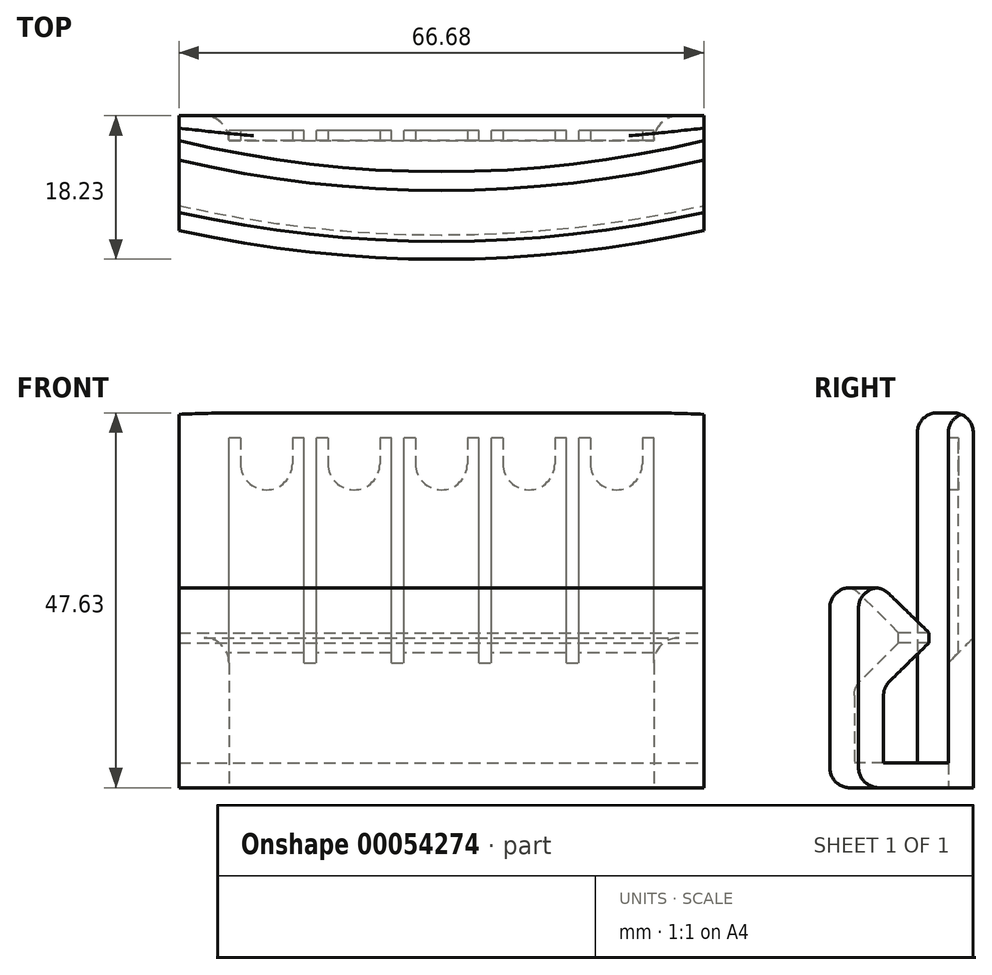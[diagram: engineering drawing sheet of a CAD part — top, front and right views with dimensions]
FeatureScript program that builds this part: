
annotation { "Feature Type Name" : "Feature", "Feature Type Description" : "" }
export const myFeature = defineFeature(function(context is Context, id is Id, definition is map)
    precondition{}
    {
        {
            var Q0;
            Q0=qCreatedBy(makeId("Top.planeOp"),FACE);
            var sketch = newSketch(context, id + "F0", { "sketchPlane" : qUnion([Q0])});
            skCircle(sketch, "E0", {"center": v(0, 0) * mm, "radius": 150.81 * mm, "construction": true});
            skCircle(sketch, "E1", {"center": v(0, 0) * mm, "radius": 142.88 * mm, "construction": true});
            skLineSegment(sketch, "E2", {"start": v(0, 0) * mm, "end": v(0, -150.81) * mm, "construction": true});
            skLineSegment(sketch, "E3", {"start": v(-17.46, -138.93) * mm, "end": v(-15.88, -138.93) * mm});
            skLineSegment(sketch, "E4", {"start": v(-15.88, -138.93) * mm, "end": v(-6.35, -138.93) * mm});
            skLineSegment(sketch, "E5", {"start": v(-6.35, -138.93) * mm, "end": v(-4.76, -138.93) * mm});
            skLineSegment(sketch, "E6", {"start": v(-4.76, -138.93) * mm, "end": v(4.76, -138.93) * mm});
            skLineSegment(sketch, "E7", {"start": v(4.76, -138.93) * mm, "end": v(6.35, -138.93) * mm});
            skLineSegment(sketch, "E8", {"start": v(6.35, -138.93) * mm, "end": v(15.88, -138.93) * mm});
            skLineSegment(sketch, "E9", {"start": v(15.88, -138.93) * mm, "end": v(17.46, -138.93) * mm});
            skLineSegment(sketch, "E10", {"start": v(17.46, -138.93) * mm, "end": v(26.99, -138.93) * mm});
            skLineSegment(sketch, "E11", {"start": v(26.99, -138.93) * mm, "end": v(33.34, -138.93) * mm});
            skLineSegment(sketch, "E12", {"start": v(-17.46, -138.93) * mm, "end": v(-26.99, -138.93) * mm});
            skLineSegment(sketch, "E13", {"start": v(-26.99, -138.93) * mm, "end": v(-33.34, -138.93) * mm});
            skLineSegment(sketch, "E14", {"start": v(-33.34, -138.93) * mm, "end": v(-33.34, -150.34) * mm});
            skLineSegment(sketch, "E15", {"start": v(33.34, -138.93) * mm, "end": v(33.34, -150.34) * mm});
            skArc(sketch, "E16", {"start": v(-33.34, -150.34) * mm, "mid": v(0, -153.99) * mm, "end": v(33.34, -150.34) * mm});
            skCircle(sketch, "E17.0", {"center": v(0, 0) * mm, "radius": 145.26 * mm, "construction": true});
            skSolve(sketch);
        }
        {
            var Q0;
            Q0 = qSketchRegion(id + "F0", true);
            extrude(context, id + "F1", {"entities" : qUnion([Q0]), "depth" : 3.17 * mm, "offsetDistance" : 25.4 * mm});
        }
        {
            var Q0;
            Q0=makeQuery(id+"F1.opExtrude","CAP_FACE",FACE,{"disambiguationData":[OSD([sQuery(id+"F0.wireOp",EDGE,"E3"),sQuery(id+"F0.wireOp",EDGE,"E4"),sQuery(id+"F0.wireOp",EDGE,"E5"),sQuery(id+"F0.wireOp",EDGE,"E6"),sQuery(id+"F0.wireOp",EDGE,"E7"),sQuery(id+"F0.wireOp",EDGE,"E8"),sQuery(id+"F0.wireOp",EDGE,"E9"),sQuery(id+"F0.wireOp",EDGE,"E10"),sQuery(id+"F0.wireOp",EDGE,"E11"),sQuery(id+"F0.wireOp",EDGE,"E12"),sQuery(id+"F0.wireOp",EDGE,"E13"),sQuery(id+"F0.wireOp",EDGE,"E14"),sQuery(id+"F0.wireOp",EDGE,"E15"),sQuery(id+"F0.wireOp",EDGE,"E16")])],"isStart":false});
            var sketch = newSketch(context, id + "F2", { "sketchPlane" : qUnion([Q0])});
            skLineSegment(sketch, "E18", {"start": v(-33.34, -150.34) * mm, "end": v(-33.34, -147.16) * mm});
            skLineSegment(sketch, "E19", {"start": v(33.34, -150.34) * mm, "end": v(33.34, -147.16) * mm});
            skArc(sketch, "E20", {"start": v(-33.34, -147.16) * mm, "mid": v(0, -150.89) * mm, "end": v(33.34, -147.16) * mm});
            skArc(sketch, "E21", {"start": v(-33.34, -150.34) * mm, "mid": v(0, -153.99) * mm, "end": v(33.34, -150.34) * mm});
            skSolve(sketch);
        }
        {
            var Q0;
            Q0 = qSketchRegion(id + "F2", true);
            extrude(context, id + "F3", {"entities" : qUnion([Q0]), "operationType" : NewBodyOperationType.ADD, "depth" : 22.22 * mm, "offsetDistance" : 25.4 * mm});
        }
        {
            var Q0;
            Q0=makeQuery(id+"F3.opExtrude","CAP_FACE",FACE,{"disambiguationData":[OSD([sQuery(id+"F2.wireOp",EDGE,"E18"),sQuery(id+"F2.wireOp",EDGE,"E19"),sQuery(id+"F2.wireOp",EDGE,"E20"),sQuery(id+"F2.wireOp",EDGE,"E21")])],"isStart":false});
            var sketch = newSketch(context, id + "F4", { "sketchPlane" : qUnion([Q0])});
            skLineSegment(sketch, "E22", {"start": v(-33.34, -147.16) * mm, "end": v(-33.34, -141.38) * mm});
            skLineSegment(sketch, "E23", {"start": v(33.34, -147.16) * mm, "end": v(33.34, -141.38) * mm});
            skArc(sketch, "E24.0", {"start": v(-33.34, -147.16) * mm, "mid": v(0, -150.89) * mm, "end": v(33.34, -147.16) * mm});
            skArc(sketch, "E25", {"start": v(-33.34, -141.38) * mm, "mid": v(0, -145.26) * mm, "end": v(33.34, -141.38) * mm});
            skSolve(sketch);
        }
        {
            var Q0;
            Q0 = qSketchRegion(id + "F4", true);
            extrude(context, id + "F5", {"entities" : qUnion([Q0]), "operationType" : NewBodyOperationType.ADD, "oppositeDirection" : true, "depth" : 12.7 * mm, "offsetDistance" : 25.4 * mm});
        }
        {
            var Q0;
            Q0=makeQuery(id+"F5.opExtrude","CAP_EDGE",EDGE,{"disambiguationData":[OSD([sQuery(id+"F4.wireOp",EDGE,"E25")])],"isStart":false});
            var Q1;
            Q1=makeQuery(id+"F5.opExtrude","CAP_EDGE",EDGE,{"disambiguationData":[OSD([sQuery(id+"F4.wireOp",EDGE,"E25")])],"isStart":true});
            chamfer(context, id + "F6", {"entities" : qUnion([Q0, Q1]), "width" : 5.7 * mm, "tangentPropagation" : true});
        }
        {
            var Q0;
            Q0=makeQuery(id+"F1.opExtrude","CAP_FACE",FACE,{"disambiguationData":[OSD([sQuery(id+"F0.wireOp",EDGE,"E3"),sQuery(id+"F0.wireOp",EDGE,"E4"),sQuery(id+"F0.wireOp",EDGE,"E5"),sQuery(id+"F0.wireOp",EDGE,"E6"),sQuery(id+"F0.wireOp",EDGE,"E7"),sQuery(id+"F0.wireOp",EDGE,"E8"),sQuery(id+"F0.wireOp",EDGE,"E9"),sQuery(id+"F0.wireOp",EDGE,"E10"),sQuery(id+"F0.wireOp",EDGE,"E11"),sQuery(id+"F0.wireOp",EDGE,"E12"),sQuery(id+"F0.wireOp",EDGE,"E13"),sQuery(id+"F0.wireOp",EDGE,"E14"),sQuery(id+"F0.wireOp",EDGE,"E15"),sQuery(id+"F0.wireOp",EDGE,"E16")])],"isStart":false});
            var sketch = newSketch(context, id + "F7", { "sketchPlane" : qUnion([Q0])});
            skLineSegment(sketch, "E26", {"start": v(-33.34, -138.93) * mm, "end": v(33.34, -138.93) * mm});
            skArc(sketch, "E27", {"start": v(-33.34, -138.93) * mm, "mid": v(0, -142.88) * mm, "end": v(33.34, -138.93) * mm});
            skSolve(sketch);
        }
        {
            var Q0;
            Q0 = qSketchRegion(id + "F7", true);
            extrude(context, id + "F8", {"entities" : qUnion([Q0]), "operationType" : NewBodyOperationType.ADD, "depth" : 44.45 * mm, "offsetDistance" : 25.4 * mm});
        }
        {
            var Q0;
            Q0=makeQuery(id+"F5.boolean.opBoolean","MERGE",FACE,{"derivedFrom":[makeQuery(id+"F3.boolean.opBoolean","MERGE",FACE,{"derivedFrom":[makeQuery(id+"F1.opExtrude","SWEPT_FACE",FACE,{"disambiguationData":[OSD([sQuery(id+"F0.wireOp",EDGE,"E15")])]}),makeQuery(id+"F3.opExtrude","SWEPT_FACE",FACE,{"disambiguationData":[OSD([sQuery(id+"F2.wireOp",EDGE,"E19")])]})]}),makeQuery(id+"F5.opExtrude","SWEPT_FACE",FACE,{"disambiguationData":[OSD([sQuery(id+"F4.wireOp",EDGE,"E23")])]})]});
            var sketch = newSketch(context, id + "F9", { "sketchPlane" : qUnion([Q0])});
            skLineSegment(sketch, "E28", {"start": v(-138.93, 15.88) * mm, "end": v(-138.93, 47.62) * mm});
            skLineSegment(sketch, "E29", {"start": v(-138.93, 47.62) * mm, "end": v(-135.76, 47.62) * mm});
            skLineSegment(sketch, "E30", {"start": v(-135.76, 47.62) * mm, "end": v(-135.76, 19.05) * mm});
            skLineSegment(sketch, "E31", {"start": v(-135.76, 19.05) * mm, "end": v(-138.93, 15.88) * mm});
            skSolve(sketch);
        }
        {
            var Q0;
            Q0 = qSketchRegion(id + "F9", true);
            var Q1;
            Q1=makeQuery(id+"F5.boolean.opBoolean","MERGE",FACE,{"derivedFrom":[makeQuery(id+"F3.boolean.opBoolean","MERGE",FACE,{"derivedFrom":[makeQuery(id+"F1.opExtrude","SWEPT_FACE",FACE,{"disambiguationData":[OSD([sQuery(id+"F0.wireOp",EDGE,"E14")])]}),makeQuery(id+"F3.opExtrude","SWEPT_FACE",FACE,{"disambiguationData":[OSD([sQuery(id+"F2.wireOp",EDGE,"E18")])]})]}),makeQuery(id+"F5.opExtrude","SWEPT_FACE",FACE,{"disambiguationData":[OSD([sQuery(id+"F4.wireOp",EDGE,"E22")])]})]});
            extrude(context, id + "F10", {"entities" : qUnion([Q0]), "operationType" : NewBodyOperationType.ADD, "endBound" : BoundingType.UP_TO_SURFACE, "oppositeDirection" : true, "depth" : 25.4 * mm, "endBoundEntityFace" : qUnion([Q1]), "offsetDistance" : 25.4 * mm});
        }
        {
            var Q0;
            Q0=makeQuery(id+"F1.opExtrude","CAP_EDGE",EDGE,{"disambiguationData":[OSD([sQuery(id+"F0.wireOp",EDGE,"E16")])],"isStart":true});
            var Q1;
            {var subQ0=sQuery(id+"F4.wireOp",EDGE,"E25");Q1=makeQuery(id+"F6.opChamfer","BLEND_EDGE",EDGE,{"blendedFrom":[makeQuery(id+"F5.opExtrude","CAP_EDGE",EDGE,{"disambiguationData":[OSD([subQ0])],"isStart":true}),makeQuery(id+"F5.boolean.opBoolean","MERGE",FACE,{"derivedFrom":[makeQuery(id+"F3.opExtrude","CAP_FACE",FACE,{"disambiguationData":[OSD([sQuery(id+"F2.wireOp",EDGE,"E18"),sQuery(id+"F2.wireOp",EDGE,"E19"),sQuery(id+"F2.wireOp",EDGE,"E20"),sQuery(id+"F2.wireOp",EDGE,"E21")])],"isStart":false}),makeQuery(id+"F5.opExtrude","CAP_FACE",FACE,{"disambiguationData":[OSD([sQuery(id+"F4.wireOp",EDGE,"E22"),sQuery(id+"F4.wireOp",EDGE,"E23"),sQuery(id+"F4.wireOp",EDGE,"E24.0"),subQ0])],"isStart":true})]})],"blendedInto":[makeQuery(id+"F5.boolean.opBoolean","MERGE",FACE,{"derivedFrom":[makeQuery(id+"F3.opExtrude","CAP_FACE",FACE,{"disambiguationData":[OSD([sQuery(id+"F2.wireOp",EDGE,"E18"),sQuery(id+"F2.wireOp",EDGE,"E19"),sQuery(id+"F2.wireOp",EDGE,"E20"),sQuery(id+"F2.wireOp",EDGE,"E21")])],"isStart":false}),makeQuery(id+"F5.opExtrude","CAP_FACE",FACE,{"disambiguationData":[OSD([sQuery(id+"F4.wireOp",EDGE,"E22"),sQuery(id+"F4.wireOp",EDGE,"E23"),sQuery(id+"F4.wireOp",EDGE,"E24.0"),subQ0])],"isStart":true})]})]});}
            var Q2;
            Q2=makeQuery(id+"F3.opExtrude","CAP_EDGE",EDGE,{"disambiguationData":[OSD([sQuery(id+"F2.wireOp",EDGE,"E21")])],"isStart":false});
            var Q3;
            Q3=makeQuery(id+"F6.opChamfer","BLEND_EDGE",EDGE,{"blendedFrom":[makeQuery(id+"F5.opExtrude","CAP_EDGE",EDGE,{"disambiguationData":[OSD([sQuery(id+"F4.wireOp",EDGE,"E25")])],"isStart":false}),makeQuery(id+"F3.opExtrude","SWEPT_FACE",FACE,{"disambiguationData":[OSD([sQuery(id+"F2.wireOp",EDGE,"E20")])]})],"blendedInto":[makeQuery(id+"F3.opExtrude","SWEPT_FACE",FACE,{"disambiguationData":[OSD([sQuery(id+"F2.wireOp",EDGE,"E20")])]})]});
            var Q4;
            Q4=makeQuery(id+"F8.opExtrude","CAP_EDGE",EDGE,{"disambiguationData":[OSD([sQuery(id+"F7.wireOp",EDGE,"E27")])],"isStart":false});
            var Q5;
            Q5=makeQuery(id+"F10.opExtrude","SWEPT_EDGE",EDGE,{"disambiguationData":[OSD([sQuery(id+"F9.wireOp",EDGE,"E29"),sQuery(id+"F9.wireOp",EDGE,"E30")])]});
            fillet(context, id + "F11", {"entities" : qUnion([Q0, Q1, Q2, Q3, Q4, Q5]), "tangentPropagation" : true, "radius" : 2.54 * mm, "defaultsChanged" : false, "vertexSettings" : [], "allowEdgeOverflow" : false});
        }
        {
            var Q0;
            Q0=makeQuery(id+"F8.boolean.opBoolean","MERGE",FACE,{"derivedFrom":[makeQuery(id+"F1.opExtrude","SWEPT_FACE",FACE,{"disambiguationData":[OSD([sQuery(id+"F0.wireOp",EDGE,"E3"),sQuery(id+"F0.wireOp",EDGE,"E4"),sQuery(id+"F0.wireOp",EDGE,"E5"),sQuery(id+"F0.wireOp",EDGE,"E6"),sQuery(id+"F0.wireOp",EDGE,"E7"),sQuery(id+"F0.wireOp",EDGE,"E8"),sQuery(id+"F0.wireOp",EDGE,"E9"),sQuery(id+"F0.wireOp",EDGE,"E10"),sQuery(id+"F0.wireOp",EDGE,"E11"),sQuery(id+"F0.wireOp",EDGE,"E12"),sQuery(id+"F0.wireOp",EDGE,"E13")])]}),makeQuery(id+"F8.opExtrude","SWEPT_FACE",FACE,{"disambiguationData":[OSD([sQuery(id+"F7.wireOp",EDGE,"E26")])]})]});
            var sketch = newSketch(context, id + "F12", { "sketchPlane" : qUnion([Q0])});
            skLineSegment(sketch, "E32.bottom", {"start": v(-33.34, 0) * mm, "end": v(-26.99, 0) * mm});
            skLineSegment(sketch, "E32.top", {"start": v(-33.34, 19.05) * mm, "end": v(-26.99, 19.05) * mm});
            skLineSegment(sketch, "E32.left", {"start": v(-33.34, 0) * mm, "end": v(-33.34, 19.05) * mm});
            skLineSegment(sketch, "E32.right", {"start": v(-26.99, 0) * mm, "end": v(-26.99, 19.05) * mm});
            skLineSegment(sketch, "E33.bottom", {"start": v(-17.46, 0) * mm, "end": v(-15.88, 0) * mm});
            skLineSegment(sketch, "E33.top", {"start": v(-17.46, 19.05) * mm, "end": v(-15.88, 19.05) * mm});
            skLineSegment(sketch, "E33.left", {"start": v(-17.46, 0) * mm, "end": v(-17.46, 19.05) * mm});
            skLineSegment(sketch, "E33.right", {"start": v(-15.88, 0) * mm, "end": v(-15.88, 19.05) * mm});
            skLineSegment(sketch, "E34.bottom", {"start": v(-6.35, 0) * mm, "end": v(-4.76, 0) * mm});
            skLineSegment(sketch, "E34.top", {"start": v(-6.35, 19.05) * mm, "end": v(-4.76, 19.05) * mm});
            skLineSegment(sketch, "E34.left", {"start": v(-6.35, 0) * mm, "end": v(-6.35, 19.05) * mm});
            skLineSegment(sketch, "E34.right", {"start": v(-4.76, 0) * mm, "end": v(-4.76, 19.05) * mm});
            skLineSegment(sketch, "E35.bottom", {"start": v(4.76, 0) * mm, "end": v(6.35, 0) * mm});
            skLineSegment(sketch, "E35.top", {"start": v(4.76, 19.05) * mm, "end": v(6.35, 19.05) * mm});
            skLineSegment(sketch, "E35.left", {"start": v(4.76, 0) * mm, "end": v(4.76, 19.05) * mm});
            skLineSegment(sketch, "E35.right", {"start": v(6.35, 0) * mm, "end": v(6.35, 19.05) * mm});
            skLineSegment(sketch, "E36.bottom", {"start": v(15.88, 0) * mm, "end": v(17.46, 0) * mm});
            skLineSegment(sketch, "E36.top", {"start": v(15.88, 19.05) * mm, "end": v(17.46, 19.05) * mm});
            skLineSegment(sketch, "E36.left", {"start": v(15.88, 0) * mm, "end": v(15.88, 19.05) * mm});
            skLineSegment(sketch, "E36.right", {"start": v(17.46, 0) * mm, "end": v(17.46, 19.05) * mm});
            skLineSegment(sketch, "E37.bottom", {"start": v(26.99, 0) * mm, "end": v(33.34, 0) * mm});
            skLineSegment(sketch, "E37.top", {"start": v(26.99, 19.05) * mm, "end": v(33.34, 19.05) * mm});
            skLineSegment(sketch, "E37.left", {"start": v(26.99, 0) * mm, "end": v(26.99, 19.05) * mm});
            skLineSegment(sketch, "E37.right", {"start": v(33.34, 0) * mm, "end": v(33.34, 19.05) * mm});
            skLineSegment(sketch, "E38", {"start": v(-26.99, 0) * mm, "end": v(-17.46, 0) * mm, "construction": true});
            skLineSegment(sketch, "E39", {"start": v(-15.88, 0) * mm, "end": v(-6.35, 0) * mm, "construction": true});
            skLineSegment(sketch, "E40", {"start": v(-4.76, 0) * mm, "end": v(4.76, 0) * mm, "construction": true});
            skLineSegment(sketch, "E41", {"start": v(6.35, 0) * mm, "end": v(15.88, 0) * mm, "construction": true});
            skLineSegment(sketch, "E42", {"start": v(17.46, 0) * mm, "end": v(26.99, 0) * mm, "construction": true});
            skSolve(sketch);
        }
        {
            var Q0;
            Q0=makeQuery(id+"F8.boolean.opBoolean","MERGE",FACE,{"derivedFrom":[makeQuery(id+"F1.opExtrude","SWEPT_FACE",FACE,{"disambiguationData":[OSD([sQuery(id+"F0.wireOp",EDGE,"E3"),sQuery(id+"F0.wireOp",EDGE,"E4"),sQuery(id+"F0.wireOp",EDGE,"E5"),sQuery(id+"F0.wireOp",EDGE,"E6"),sQuery(id+"F0.wireOp",EDGE,"E7"),sQuery(id+"F0.wireOp",EDGE,"E8"),sQuery(id+"F0.wireOp",EDGE,"E9"),sQuery(id+"F0.wireOp",EDGE,"E10"),sQuery(id+"F0.wireOp",EDGE,"E11"),sQuery(id+"F0.wireOp",EDGE,"E12"),sQuery(id+"F0.wireOp",EDGE,"E13")])]}),makeQuery(id+"F8.opExtrude","SWEPT_FACE",FACE,{"disambiguationData":[OSD([sQuery(id+"F7.wireOp",EDGE,"E26")])]})]});
            var sketch = newSketch(context, id + "F13", { "sketchPlane" : qUnion([Q0])});
            skLineSegment(sketch, "E43", {"start": v(-26.99, 20.64) * mm, "end": v(-26.99, 44.45) * mm, "construction": true});
            skLineSegment(sketch, "E44", {"start": v(-26.99, 44.45) * mm, "end": v(-17.46, 20.64) * mm, "construction": true});
            skLineSegment(sketch, "E45", {"start": v(-26.99, 20.64) * mm, "end": v(-17.46, 20.64) * mm, "construction": true});
            skLineSegment(sketch, "E46.bottom", {"start": v(-26.99, 15.88) * mm, "end": v(-17.46, 15.88) * mm});
            skLineSegment(sketch, "E46.top", {"start": v(-26.99, 44.45) * mm, "end": v(-25.53, 44.45) * mm});
            skLineSegment(sketch, "E46.left", {"start": v(-26.99, 15.88) * mm, "end": v(-26.99, 44.45) * mm});
            skLineSegment(sketch, "E46.right", {"start": v(-17.46, 15.88) * mm, "end": v(-17.46, 44.45) * mm});
            skArc(sketch, "E47", {"start": v(-25.53, 41.15) * mm, "mid": v(-22.23, 37.85) * mm, "end": v(-18.92, 41.15) * mm});
            skPoint(sketch, "E47.centerSnap0", {"position": v(-22.23, 44.45) * mm});
            skLineSegment(sketch, "E48", {"start": v(-22.23, 44.45) * mm, "end": v(-22.23, 41.15) * mm, "construction": true});
            skLineSegment(sketch, "E49.left", {"start": v(-25.53, 44.45) * mm, "end": v(-25.53, 41.15) * mm});
            skLineSegment(sketch, "E49.right", {"start": v(-18.92, 44.45) * mm, "end": v(-18.92, 41.15) * mm});
            skLineSegment(sketch, "E50.trimOffspring", {"start": v(-18.92, 44.45) * mm, "end": v(-17.46, 44.45) * mm});
            skLineSegment(sketch, "E51.1.0.0", {"start": v(-15.88, 15.88) * mm, "end": v(-6.35, 15.88) * mm});
            skLineSegment(sketch, "E51.1.0.1", {"start": v(-6.35, 15.88) * mm, "end": v(-6.35, 44.45) * mm});
            skLineSegment(sketch, "E51.1.0.2", {"start": v(-15.88, 15.88) * mm, "end": v(-15.88, 44.45) * mm});
            skLineSegment(sketch, "E51.1.0.3", {"start": v(-7.81, 44.45) * mm, "end": v(-6.35, 44.45) * mm});
            skLineSegment(sketch, "E51.1.0.4", {"start": v(-7.81, 44.45) * mm, "end": v(-7.81, 41.15) * mm});
            skArc(sketch, "E51.1.0.5", {"start": v(-14.41, 41.15) * mm, "mid": v(-11.11, 37.85) * mm, "end": v(-7.81, 41.15) * mm});
            skLineSegment(sketch, "E51.1.0.6", {"start": v(-14.41, 44.45) * mm, "end": v(-14.41, 41.15) * mm});
            skLineSegment(sketch, "E51.1.0.7", {"start": v(-15.88, 44.45) * mm, "end": v(-14.41, 44.45) * mm});
            skLineSegment(sketch, "E51.2.0.0", {"start": v(-4.76, 15.88) * mm, "end": v(4.76, 15.88) * mm});
            skLineSegment(sketch, "E51.2.0.1", {"start": v(4.76, 15.88) * mm, "end": v(4.76, 44.45) * mm});
            skLineSegment(sketch, "E51.2.0.2", {"start": v(-4.76, 15.88) * mm, "end": v(-4.76, 44.45) * mm});
            skLineSegment(sketch, "E51.2.0.3", {"start": v(3.3, 44.45) * mm, "end": v(4.76, 44.45) * mm});
            skLineSegment(sketch, "E51.2.0.4", {"start": v(3.3, 44.45) * mm, "end": v(3.3, 41.15) * mm});
            skArc(sketch, "E51.2.0.5", {"start": v(-3.3, 41.15) * mm, "mid": v(0, 37.85) * mm, "end": v(3.3, 41.15) * mm});
            skLineSegment(sketch, "E51.2.0.6", {"start": v(-3.3, 44.45) * mm, "end": v(-3.3, 41.15) * mm});
            skLineSegment(sketch, "E51.2.0.7", {"start": v(-4.76, 44.45) * mm, "end": v(-3.3, 44.45) * mm});
            skLineSegment(sketch, "E51.3.0.0", {"start": v(6.35, 15.88) * mm, "end": v(15.88, 15.88) * mm});
            skLineSegment(sketch, "E51.3.0.1", {"start": v(15.88, 15.88) * mm, "end": v(15.88, 44.45) * mm});
            skLineSegment(sketch, "E51.3.0.2", {"start": v(6.35, 15.88) * mm, "end": v(6.35, 44.45) * mm});
            skLineSegment(sketch, "E51.3.0.3", {"start": v(14.41, 44.45) * mm, "end": v(15.88, 44.45) * mm});
            skLineSegment(sketch, "E51.3.0.4", {"start": v(14.41, 44.45) * mm, "end": v(14.41, 41.15) * mm});
            skArc(sketch, "E51.3.0.5", {"start": v(7.81, 41.15) * mm, "mid": v(11.11, 37.85) * mm, "end": v(14.41, 41.15) * mm});
            skLineSegment(sketch, "E51.3.0.6", {"start": v(7.81, 44.45) * mm, "end": v(7.81, 41.15) * mm});
            skLineSegment(sketch, "E51.3.0.7", {"start": v(6.35, 44.45) * mm, "end": v(7.81, 44.45) * mm});
            skLineSegment(sketch, "E51.4.0.0", {"start": v(17.46, 15.88) * mm, "end": v(26.99, 15.88) * mm});
            skLineSegment(sketch, "E51.4.0.1", {"start": v(26.99, 15.88) * mm, "end": v(26.99, 44.45) * mm});
            skLineSegment(sketch, "E51.4.0.2", {"start": v(17.46, 15.88) * mm, "end": v(17.46, 44.45) * mm});
            skLineSegment(sketch, "E51.4.0.3", {"start": v(25.53, 44.45) * mm, "end": v(26.99, 44.45) * mm});
            skLineSegment(sketch, "E51.4.0.4", {"start": v(25.53, 44.45) * mm, "end": v(25.53, 41.15) * mm});
            skArc(sketch, "E51.4.0.5", {"start": v(18.92, 41.15) * mm, "mid": v(22.22, 37.85) * mm, "end": v(25.53, 41.15) * mm});
            skLineSegment(sketch, "E51.4.0.6", {"start": v(18.92, 44.45) * mm, "end": v(18.92, 41.15) * mm});
            skLineSegment(sketch, "E51.4.0.7", {"start": v(17.46, 44.45) * mm, "end": v(18.92, 44.45) * mm});
            skLineSegment(sketch, "E51.direction1", {"start": v(-26.99, 15.88) * mm, "end": v(-15.88, 15.88) * mm, "construction": true});
            skSolve(sketch);
        }
        {
            var Q0;
            Q0 = qSketchRegion(id + "F13", true);
            extrude(context, id + "F14", {"entities" : qUnion([Q0]), "operationType" : NewBodyOperationType.REMOVE, "depth" : 1.27 * mm, "offsetDistance" : 25.4 * mm});
        }
        {
            var Q0;
            Q0=makeQuery(id+"F1.opExtrude","CAP_FACE",FACE,{"disambiguationData":[OSD([sQuery(id+"F0.wireOp",EDGE,"E3"),sQuery(id+"F0.wireOp",EDGE,"E4"),sQuery(id+"F0.wireOp",EDGE,"E5"),sQuery(id+"F0.wireOp",EDGE,"E6"),sQuery(id+"F0.wireOp",EDGE,"E7"),sQuery(id+"F0.wireOp",EDGE,"E8"),sQuery(id+"F0.wireOp",EDGE,"E9"),sQuery(id+"F0.wireOp",EDGE,"E10"),sQuery(id+"F0.wireOp",EDGE,"E11"),sQuery(id+"F0.wireOp",EDGE,"E12"),sQuery(id+"F0.wireOp",EDGE,"E13"),sQuery(id+"F0.wireOp",EDGE,"E14"),sQuery(id+"F0.wireOp",EDGE,"E15"),sQuery(id+"F0.wireOp",EDGE,"E16")])],"isStart":true});
            var sketch = newSketch(context, id + "F15", { "sketchPlane" : qUnion([Q0])});
            skLineSegment(sketch, "E52", {"start": v(0, 135.55) * mm, "end": v(0, 156.37) * mm, "construction": true});
            skPoint(sketch, "E52.startSnap0", {"position": v(0, 138.93) * mm});
            skLineSegment(sketch, "E53", {"start": v(-33.34, 138.93) * mm, "end": v(-26.99, 138.93) * mm});
            skLineSegment(sketch, "E54", {"start": v(-33.34, 138.93) * mm, "end": v(-33.34, 135.76) * mm});
            skLineSegment(sketch, "E55", {"start": v(-33.34, 135.76) * mm, "end": v(-30.16, 135.76) * mm});
            skArc(sketch, "E56", {"start": v(-30.16, 135.76) * mm, "mid": v(-27.92, 136.69) * mm, "end": v(-26.99, 138.93) * mm});
            skPoint(sketch, "E56.startSnap0", {"position": v(-30.16, 138.93) * mm});
            skLineSegment(sketch, "E57.MirrorCS", {"start": v(33.34, 135.76) * mm, "end": v(30.16, 135.76) * mm});
            skLineSegment(sketch, "E58.MirrorCS", {"start": v(33.34, 138.93) * mm, "end": v(33.34, 135.76) * mm});
            skLineSegment(sketch, "E59.MirrorCS", {"start": v(33.34, 138.93) * mm, "end": v(26.99, 138.93) * mm});
            skArc(sketch, "E60.MirrorCS", {"start": v(30.16, 135.76) * mm, "mid": v(27.92, 136.69) * mm, "end": v(26.99, 138.93) * mm});
            skSolve(sketch);
        }
        {
            var Q0;
            Q0 = qSketchRegion(id + "F15", true);
            extrude(context, id + "F16", {"entities" : qUnion([Q0]), "operationType" : NewBodyOperationType.ADD, "endBound" : BoundingType.UP_TO_NEXT, "oppositeDirection" : true, "depth" : 25.4 * mm, "offsetDistance" : 25.4 * mm});
        }
    });
